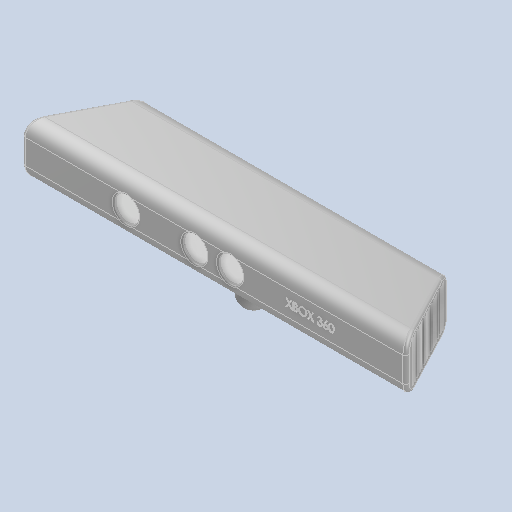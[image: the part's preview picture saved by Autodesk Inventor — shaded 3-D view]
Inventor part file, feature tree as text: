
AUTODESK INVENTOR PART (.ipt)
format: ipt  version: 2024 (Build 280153000, 153)  size: 481,280 bytes
history: native  units: in
note: dims shown in document units (in); Inventor stores cm internally (conversion verified against a paired STEP export)
features: other x1, fillet x1
ambient origin geometry x8: Origin, YZ Plane, XZ Plane, XY Plane, X Axis, Y Axis, Z Axis, Center Point
bodies: Solid1 (feature_tree)
feature tree (2):
  other  "Plane1"
  fillet  "Fillet3"  [1 undecoded]
note: 1 required parameter value undecoded (feature->parameter linkage not recoverable at this tier; creation-order binding heuristic only, values carry confidence <= 0.55)
